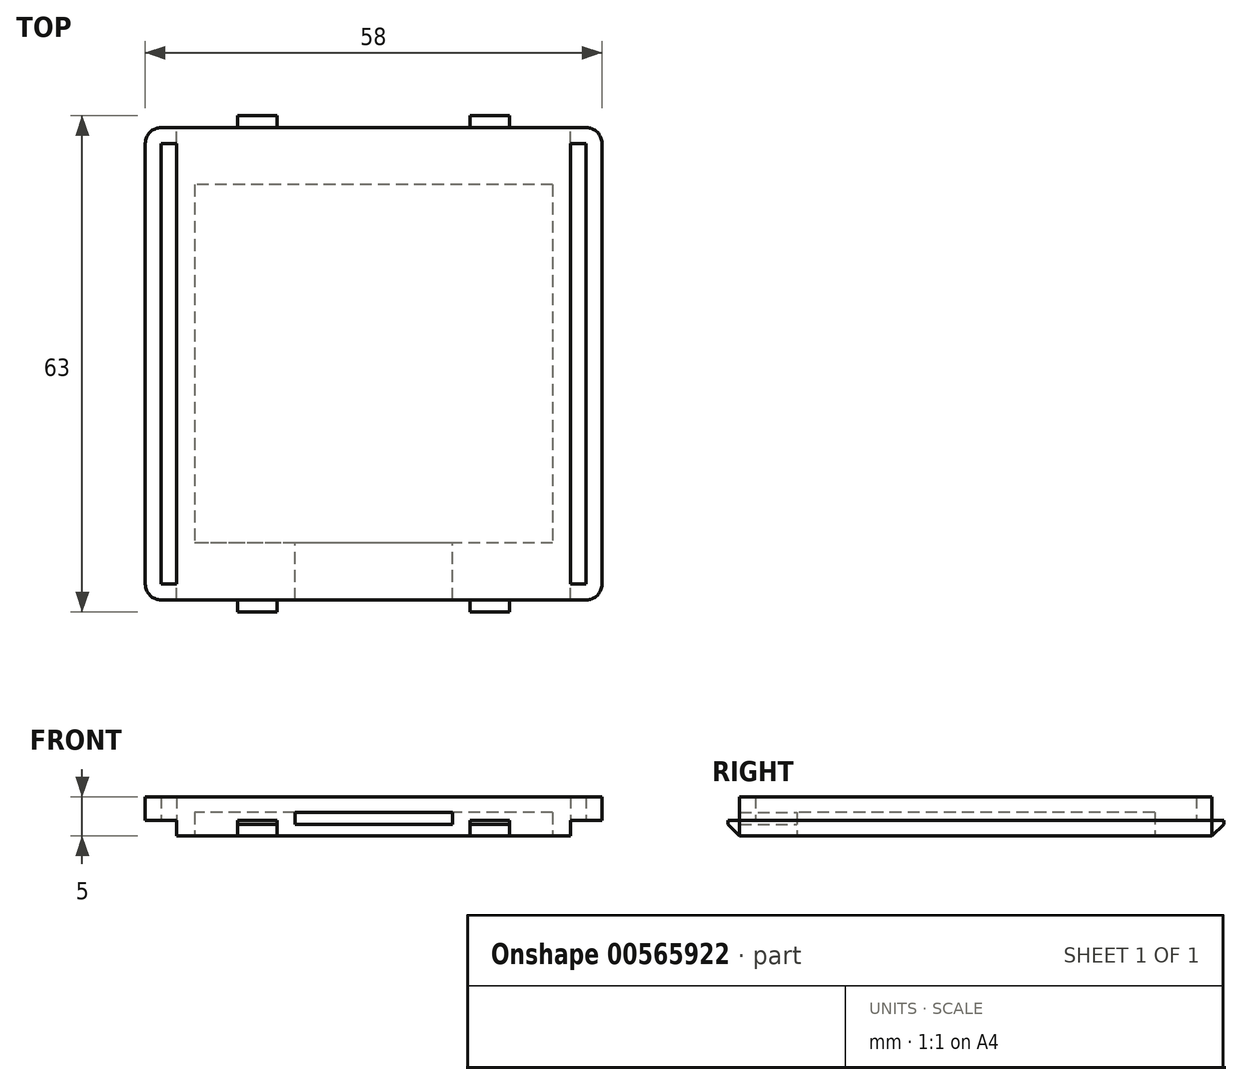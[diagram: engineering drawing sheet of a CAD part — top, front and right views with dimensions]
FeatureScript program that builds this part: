
annotation { "Feature Type Name" : "Feature", "Feature Type Description" : "" }
export const myFeature = defineFeature(function(context is Context, id is Id, definition is map)
    precondition{}
    {
        {
            var Q0;
            Q0=qCreatedBy(makeId("Top.planeOp"),FACE);
            var sketch = newSketch(context, id + "F0", { "sketchPlane" : qUnion([Q0])});
            skLineSegment(sketch, "E0.bottom", {"start": v(25, -30) * mm, "end": v(-25, -30) * mm});
            skLineSegment(sketch, "E0.top", {"start": v(25, 30) * mm, "end": v(-25, 30) * mm});
            skLineSegment(sketch, "E0.left", {"start": v(25, -30) * mm, "end": v(25, 30) * mm});
            skLineSegment(sketch, "E0.right", {"start": v(-25, -30) * mm, "end": v(-25, 30) * mm});
            skPoint(sketch, "E0.middle", {"position": v(0, 0) * mm});
            skSolve(sketch);
        }
        {
            var Q0;
            Q0 = qSketchRegion(id + "F0", true);
            extrude(context, id + "F1", {"entities" : qUnion([Q0]), "depth" : 5 * mm, "offsetDistance" : 25 * mm});
        }
        {
            var Q0;
            Q0=qCreatedBy(makeId("Top.planeOp"),FACE);
            var sketch = newSketch(context, id + "F2", { "sketchPlane" : qUnion([Q0])});
            skLineSegment(sketch, "E1.bottom", {"start": v(22.75, 22.75) * mm, "end": v(-22.75, 22.75) * mm});
            skLineSegment(sketch, "E1.top", {"start": v(22.75, -22.75) * mm, "end": v(-22.75, -22.75) * mm});
            skLineSegment(sketch, "E1.left", {"start": v(22.75, 22.75) * mm, "end": v(22.75, -22.75) * mm});
            skLineSegment(sketch, "E1.right", {"start": v(-22.75, 22.75) * mm, "end": v(-22.75, -22.75) * mm});
            skPoint(sketch, "E1.middle", {"position": v(0, 0) * mm});
            skSolve(sketch);
        }
        {
            var Q0;
            Q0=qCreatedBy(makeId("Top.planeOp"),FACE);
            var sketch = newSketch(context, id + "F3", { "sketchPlane" : qUnion([Q0])});
            skLineSegment(sketch, "E2.bottom", {"start": v(29, 30) * mm, "end": v(-29, 30) * mm});
            skLineSegment(sketch, "E2.top", {"start": v(29, -30) * mm, "end": v(-29, -30) * mm});
            skLineSegment(sketch, "E2.left", {"start": v(29, 30) * mm, "end": v(29, -30) * mm});
            skLineSegment(sketch, "E2.right", {"start": v(-29, 30) * mm, "end": v(-29, -30) * mm});
            skPoint(sketch, "E2.middle", {"position": v(0, 0) * mm});
            skSolve(sketch);
        }
        {
            var Q0;
            Q0=makeQuery(id+"F3.imprint","IMPRINT",FACE,{"disambiguationData":[TD([[makeQuery(id+"F3.imprint","IMPRINT",EDGE,{"derivedFrom":sQuery(id+"F3.wireOp",EDGE,"E2.bottom")}),1.0]])]});
            extrude(context, id + "F4", {"entities" : qUnion([Q0]), "operationType" : NewBodyOperationType.ADD, "depth" : 5 * mm, "offsetDistance" : 25 * mm, "hasSecondDirection" : true, "secondDirectionOppositeDirection" : false, "secondDirectionDepth" : 2 * mm});
        }
        {
            var Q0;
            Q0 = qSketchRegion(id + "F2", true);
            extrude(context, id + "F5", {"entities" : qUnion([Q0]), "operationType" : NewBodyOperationType.REMOVE, "depth" : 3 * mm, "offsetDistance" : 25 * mm});
        }
        {
            var Q0;
            Q0=qCreatedBy(makeId("Top.planeOp"),FACE);
            var sketch = newSketch(context, id + "F6", { "sketchPlane" : qUnion([Q0])});
            skLineSegment(sketch, "E3.bottom", {"start": v(10, -30) * mm, "end": v(-10, -30) * mm});
            skLineSegment(sketch, "E3.top", {"start": v(10, 0) * mm, "end": v(-10, 0) * mm});
            skLineSegment(sketch, "E3.left", {"start": v(10, -30) * mm, "end": v(10, 0) * mm});
            skLineSegment(sketch, "E3.right", {"start": v(-10, -30) * mm, "end": v(-10, 0) * mm});
            skPoint(sketch, "E3.middle", {"position": v(0, -15) * mm});
            skSolve(sketch);
        }
        {
            var Q0;
            Q0 = qSketchRegion(id + "F6", true);
            extrude(context, id + "F7", {"entities" : qUnion([Q0]), "operationType" : NewBodyOperationType.REMOVE, "depth" : 3 * mm, "offsetDistance" : 25 * mm, "hasSecondDirection" : true, "secondDirectionOppositeDirection" : false, "secondDirectionDepth" : 1.5 * mm});
        }
        {
            var Q0;
            Q0=qCreatedBy(makeId("Top.planeOp"),FACE);
            var sketch = newSketch(context, id + "F8", { "sketchPlane" : qUnion([Q0])});
            skLineSegment(sketch, "E4.bottom", {"start": v(-25, 28) * mm, "end": v(-27, 28) * mm});
            skLineSegment(sketch, "E4.top", {"start": v(-25, -28) * mm, "end": v(-27, -28) * mm});
            skLineSegment(sketch, "E4.left", {"start": v(-25, 28) * mm, "end": v(-25, -28) * mm});
            skLineSegment(sketch, "E4.right", {"start": v(-27, 28) * mm, "end": v(-27, -28) * mm});
            skLineSegment(sketch, "E5.bottom", {"start": v(25, 28) * mm, "end": v(27, 28) * mm});
            skLineSegment(sketch, "E5.top", {"start": v(25, -28) * mm, "end": v(27, -28) * mm});
            skLineSegment(sketch, "E5.left", {"start": v(25, 28) * mm, "end": v(25, -28) * mm});
            skLineSegment(sketch, "E5.right", {"start": v(27, 28) * mm, "end": v(27, -28) * mm});
            skSolve(sketch);
        }
        {
            var Q0;
            Q0 = qSketchRegion(id + "F8", true);
            extrude(context, id + "F9", {"entities" : qUnion([Q0]), "operationType" : NewBodyOperationType.REMOVE, "depth" : 25 * mm, "offsetDistance" : 25 * mm});
        }
        {
            var Q0;
            Q0=makeQuery(id+"F4.opExtrude","SWEPT_EDGE",EDGE,{"disambiguationData":[OSD([sQuery(id+"F3.wireOp",EDGE,"E2.top"),sQuery(id+"F3.wireOp",EDGE,"E2.left")])]});
            var Q1;
            Q1=makeQuery(id+"F4.opExtrude","SWEPT_EDGE",EDGE,{"disambiguationData":[OSD([sQuery(id+"F3.wireOp",EDGE,"E2.top"),sQuery(id+"F3.wireOp",EDGE,"E2.right")])]});
            var Q2;
            Q2=makeQuery(id+"F4.opExtrude","SWEPT_EDGE",EDGE,{"disambiguationData":[OSD([sQuery(id+"F3.wireOp",EDGE,"E2.bottom"),sQuery(id+"F3.wireOp",EDGE,"E2.right")])]});
            var Q3;
            Q3=makeQuery(id+"F4.opExtrude","SWEPT_EDGE",EDGE,{"disambiguationData":[OSD([sQuery(id+"F3.wireOp",EDGE,"E2.bottom"),sQuery(id+"F3.wireOp",EDGE,"E2.left")])]});
            fillet(context, id + "F10", {"entities" : qUnion([Q0, Q1, Q2, Q3]), "radius" : 2 * mm, "tangentPropagation" : true, "allowEdgeOverflow" : false});
        }
        {
            var Q0;
            Q0=qCreatedBy(makeId("Top.planeOp"),FACE);
            var sketch = newSketch(context, id + "F11", { "sketchPlane" : qUnion([Q0])});
            skLineSegment(sketch, "E6.bottom", {"start": v(-17.25, -30) * mm, "end": v(-12.25, -30) * mm});
            skLineSegment(sketch, "E6.top", {"start": v(-17.25, -31.5) * mm, "end": v(-12.25, -31.5) * mm});
            skLineSegment(sketch, "E6.left", {"start": v(-17.25, -30) * mm, "end": v(-17.25, -31.5) * mm});
            skLineSegment(sketch, "E6.right", {"start": v(-12.25, -30) * mm, "end": v(-12.25, -31.5) * mm});
            skLineSegment(sketch, "E7.MirrorCS", {"start": v(17.25, -30) * mm, "end": v(12.25, -30) * mm});
            skLineSegment(sketch, "E8.MirrorCS", {"start": v(17.25, -31.5) * mm, "end": v(12.25, -31.5) * mm});
            skLineSegment(sketch, "E9.MirrorCS", {"start": v(17.25, -30) * mm, "end": v(17.25, -31.5) * mm});
            skLineSegment(sketch, "E10.MirrorCS", {"start": v(12.25, -30) * mm, "end": v(12.25, -31.5) * mm});
            skLineSegment(sketch, "E11.MirrorCS", {"start": v(12.25, 30) * mm, "end": v(12.25, 31.5) * mm});
            skLineSegment(sketch, "E12.MirrorCS", {"start": v(17.25, 30) * mm, "end": v(17.25, 31.5) * mm});
            skLineSegment(sketch, "E13.MirrorCS", {"start": v(-12.25, 30) * mm, "end": v(-12.25, 31.5) * mm});
            skLineSegment(sketch, "E14.MirrorCS", {"start": v(-17.25, 30) * mm, "end": v(-17.25, 31.5) * mm});
            skLineSegment(sketch, "E15.MirrorCS", {"start": v(17.25, 31.5) * mm, "end": v(12.25, 31.5) * mm});
            skLineSegment(sketch, "E16.MirrorCS", {"start": v(-17.25, 31.5) * mm, "end": v(-12.25, 31.5) * mm});
            skLineSegment(sketch, "E17.MirrorCS", {"start": v(-17.25, 30) * mm, "end": v(-12.25, 30) * mm});
            skLineSegment(sketch, "E18.MirrorCS", {"start": v(17.25, 30) * mm, "end": v(12.25, 30) * mm});
            skSolve(sketch);
        }
        {
            var Q0;
            Q0 = qSketchRegion(id + "F11", true);
            extrude(context, id + "F12", {"entities" : qUnion([Q0]), "operationType" : NewBodyOperationType.ADD, "depth" : 2 * mm, "offsetDistance" : 25 * mm});
        }
        {
            var Q0;
            Q0=makeQuery(id+"F12.opExtrude","CAP_EDGE",EDGE,{"disambiguationData":[OSD([sQuery(id+"F11.wireOp",EDGE,"E6.top")])],"isStart":true});
            var Q1;
            Q1=makeQuery(id+"F12.opExtrude","CAP_EDGE",EDGE,{"disambiguationData":[OSD([sQuery(id+"F11.wireOp",EDGE,"E8.MirrorCS")])],"isStart":true});
            var Q2;
            Q2=makeQuery(id+"F12.opExtrude","CAP_EDGE",EDGE,{"disambiguationData":[OSD([sQuery(id+"F11.wireOp",EDGE,"E15.MirrorCS")])],"isStart":true});
            var Q3;
            Q3=makeQuery(id+"F12.opExtrude","CAP_EDGE",EDGE,{"disambiguationData":[OSD([sQuery(id+"F11.wireOp",EDGE,"E16.MirrorCS")])],"isStart":true});
            chamfer(context, id + "F13", {"entities" : qUnion([Q0, Q1, Q2, Q3]), "width" : 1.5 * mm, "tangentPropagation" : true});
        }
    });
